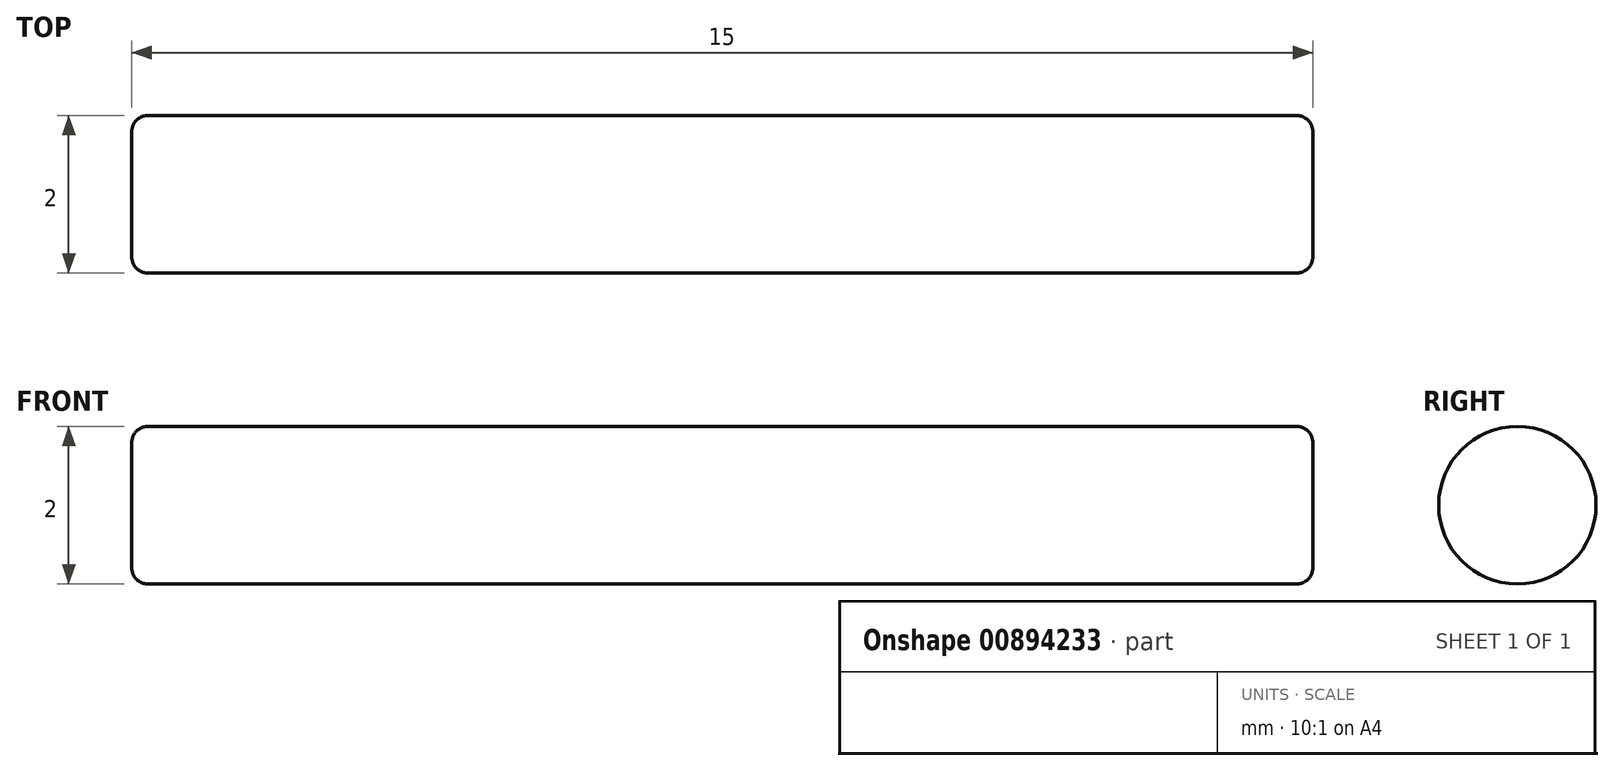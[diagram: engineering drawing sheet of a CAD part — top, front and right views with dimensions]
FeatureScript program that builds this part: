
annotation { "Feature Type Name" : "Feature", "Feature Type Description" : "" }
export const myFeature = defineFeature(function(context is Context, id is Id, definition is map)
    precondition{}
    {
        {
            var Q0;
            Q0=qCreatedBy(makeId("Front.planeOp"),FACE);
            var sketch = newSketch(context, id + "F0", { "sketchPlane" : qUnion([Q0])});
            skLineSegment(sketch, "E0", {"start": v(0, 0) * mm, "end": v(0, 0.8) * mm});
            skLineSegment(sketch, "E1", {"start": v(0.2, 1) * mm, "end": v(14.8, 1) * mm});
            skLineSegment(sketch, "E2", {"start": v(15, 0.8) * mm, "end": v(15, 0) * mm});
            skLineSegment(sketch, "E3", {"start": v(15, 0) * mm, "end": v(0, 0) * mm});
            skPoint(sketch, "E4.visualSharp", {"position": v(15, 1) * mm});
            skArc(sketch, "E4.filletArc", {"start": v(15, 0.8) * mm, "mid": v(14.94, 0.94) * mm, "end": v(14.8, 1) * mm});
            skPoint(sketch, "E5.visualSharp", {"position": v(0, 1) * mm});
            skArc(sketch, "E5.filletArc", {"start": v(0.2, 1) * mm, "mid": v(0.06, 0.94) * mm, "end": v(0, 0.8) * mm});
            skSolve(sketch);
        }
        {
            var Q0;
            Q0=makeQuery(id+"F0.imprint","IMPRINT",FACE,{"disambiguationData":[TD([[makeQuery(id+"F0.imprint","IMPRINT",EDGE,{"derivedFrom":sQuery(id+"F0.wireOp",EDGE,"E0")}),-1.0]])]});
            var Q1;
            Q1=sQuery(id+"F0.wireOp",EDGE,"E3");
            revolve(context, id + "F1", {"surfaceOperationType" : NewSurfaceOperationType.NEW, "entities" : qUnion([Q0]), "axis" : qUnion([Q1]), "revolveType" : RevolveType.FULL});
        }
    });
